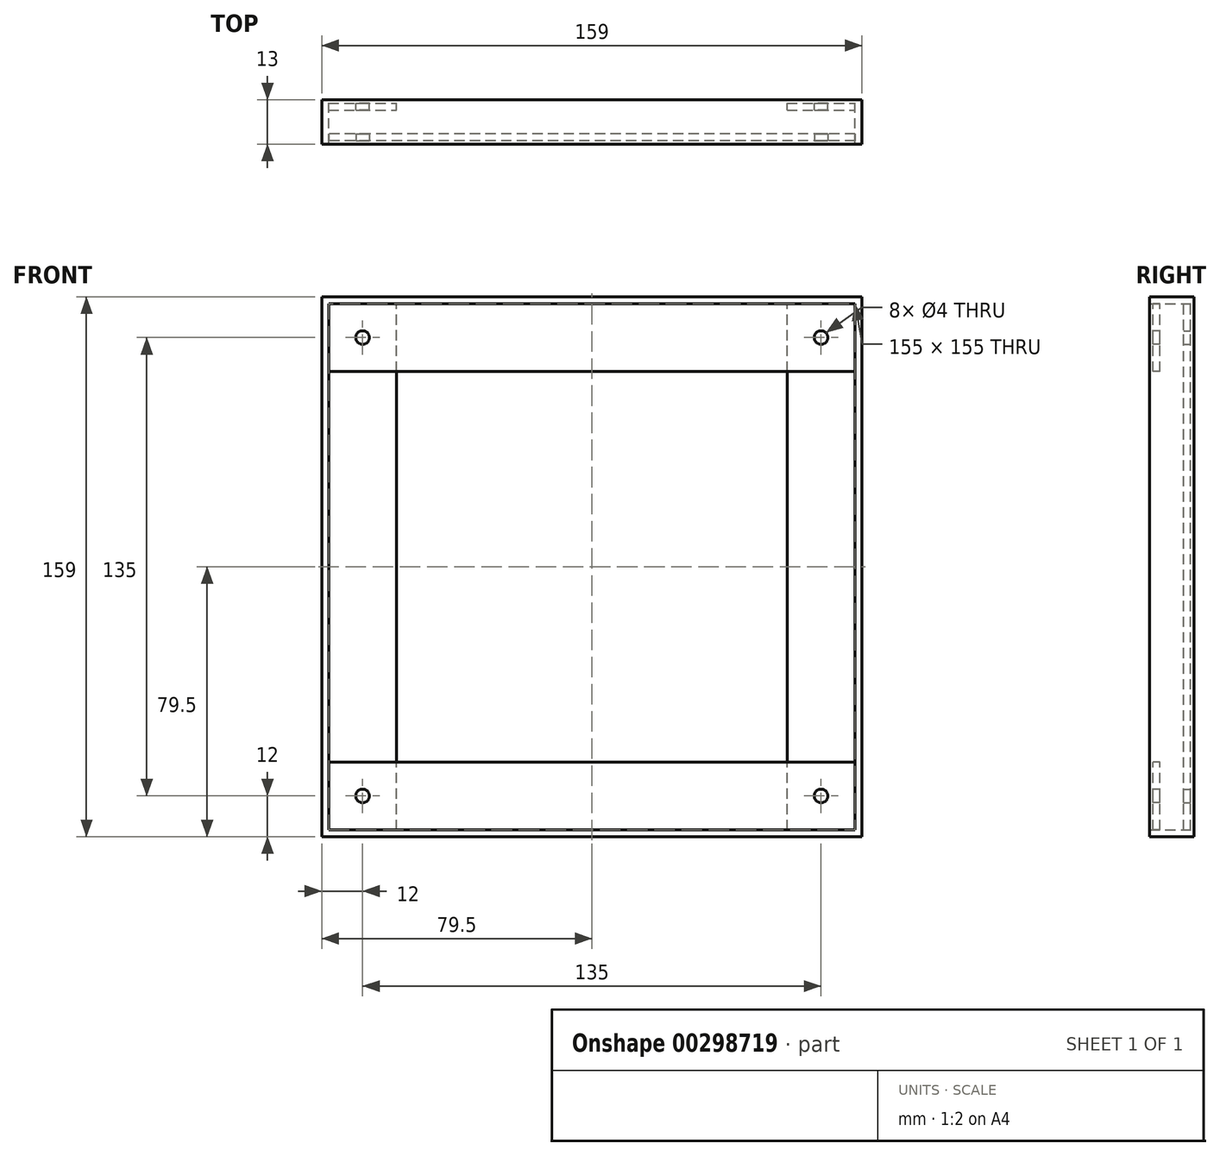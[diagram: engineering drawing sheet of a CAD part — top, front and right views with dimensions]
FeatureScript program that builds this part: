
annotation { "Feature Type Name" : "Feature", "Feature Type Description" : "" }
export const myFeature = defineFeature(function(context is Context, id is Id, definition is map)
    precondition{}
    {
        {
            var Q0;
            Q0=qCreatedBy(makeId("Front.planeOp"),FACE);
            var sketch = newSketch(context, id + "F0", { "sketchPlane" : qUnion([Q0])});
            skLineSegment(sketch, "E0.bottom", {"start": v(0, 0) * mm, "end": v(155, 0) * mm});
            skLineSegment(sketch, "E0.top", {"start": v(0, 155) * mm, "end": v(155, 155) * mm});
            skLineSegment(sketch, "E0.left", {"start": v(0, 0) * mm, "end": v(0, 155) * mm});
            skLineSegment(sketch, "E0.right", {"start": v(155, 0) * mm, "end": v(155, 155) * mm});
            skLineSegment(sketch, "E1.bottom", {"start": v(-2, 157) * mm, "end": v(157, 157) * mm});
            skLineSegment(sketch, "E1.top", {"start": v(-2, -2) * mm, "end": v(157, -2) * mm});
            skLineSegment(sketch, "E1.left", {"start": v(-2, 157) * mm, "end": v(-2, -2) * mm});
            skLineSegment(sketch, "E1.right", {"start": v(157, 157) * mm, "end": v(157, -2) * mm});
            skSolve(sketch);
        }
        {
            var Q0;
            Q0=makeQuery(id+"F0.imprint","IMPRINT",FACE,{"disambiguationData":[TD([[makeQuery(id+"F0.imprint","IMPRINT",EDGE,{"derivedFrom":sQuery(id+"F0.wireOp",EDGE,"E0.bottom")}),-1.0]])]});
            extrude(context, id + "F1", {"entities" : qUnion([Q0]), "depth" : 13 * mm});
        }
        {
            var Q0;
            Q0=qCreatedBy(makeId("Front.planeOp"),FACE);
            cPlane(context, id + "F2", {"entities" : qUnion([Q0]), "cplaneType" : CPlaneType.OFFSET, "offset" : 1 * mm, "width" : 150 * mm, "height" : 150 * mm});
        }
        {
            var Q0;
            Q0=qCreatedBy(id+"F2.planeOp",FACE);
            var sketch = newSketch(context, id + "F3", { "sketchPlane" : qUnion([Q0])});
            skLineSegment(sketch, "E2.0", {"start": v(0, 155) * mm, "end": v(155, 155) * mm});
            skLineSegment(sketch, "E2.1", {"start": v(0, 0) * mm, "end": v(0, 155) * mm});
            skLineSegment(sketch, "E2.2", {"start": v(0, 0) * mm, "end": v(155, 0) * mm});
            skLineSegment(sketch, "E2.3", {"start": v(155, 0) * mm, "end": v(155, 155) * mm});
            skLineSegment(sketch, "E3", {"start": v(20, 0) * mm, "end": v(20, 155) * mm});
            skCircle(sketch, "E4", {"center": v(10, 145) * mm, "radius": 2 * mm});
            skCircle(sketch, "E5", {"center": v(10, 10) * mm, "radius": 2 * mm});
            skLineSegment(sketch, "E6", {"start": v(0, 77.5) * mm, "end": v(155, 77.5) * mm, "construction": true});
            skLineSegment(sketch, "E7", {"start": v(77.5, 0) * mm, "end": v(77.5, 155) * mm, "construction": true});
            skLineSegment(sketch, "E8", {"start": v(135, 0) * mm, "end": v(135, 155) * mm});
            skCircle(sketch, "E9", {"center": v(145, 10) * mm, "radius": 2 * mm});
            skCircle(sketch, "E10", {"center": v(145, 145) * mm, "radius": 2 * mm});
            skSolve(sketch);
        }
        {
            var Q0;
            {var subQ1=sQuery(id+"F3.wireOp",EDGE,"E2.1");Q0=makeQuery(id+"F3.imprint","IMPRINT",FACE,{"disambiguationData":[TD([[makeQuery(id+"F3.imprint","IMPRINT",EDGE,{"derivedFrom":subQ1}),-1.0]])]});}
            var Q1;
            {var subQ1=sQuery(id+"F3.wireOp",EDGE,"E2.3");Q1=makeQuery(id+"F3.imprint","IMPRINT",FACE,{"disambiguationData":[TD([[makeQuery(id+"F3.imprint","IMPRINT",EDGE,{"derivedFrom":subQ1}),1.0]])]});}
            extrude(context, id + "F4", {"entities" : qUnion([Q0, Q1]), "depth" : 2 * mm});
        }
        {
            var Q0;
            Q0=makeQuery(id+"F1.opExtrude","CAP_FACE",FACE,{"disambiguationData":[OSD([sQuery(id+"F0.wireOp",EDGE,"E0.bottom"),sQuery(id+"F0.wireOp",EDGE,"E0.top"),sQuery(id+"F0.wireOp",EDGE,"E0.left"),sQuery(id+"F0.wireOp",EDGE,"E0.right"),sQuery(id+"F0.wireOp",EDGE,"E1.bottom"),sQuery(id+"F0.wireOp",EDGE,"E1.top"),sQuery(id+"F0.wireOp",EDGE,"E1.left"),sQuery(id+"F0.wireOp",EDGE,"E1.right")])],"isStart":false});
            cPlane(context, id + "F5", {"entities" : qUnion([Q0]), "cplaneType" : CPlaneType.OFFSET, "offset" : 1 * mm, "oppositeDirection" : true, "width" : 150 * mm, "height" : 150 * mm});
        }
        {
            var Q0;
            Q0=qCreatedBy(id+"F5.planeOp",FACE);
            var sketch = newSketch(context, id + "F6", { "sketchPlane" : qUnion([Q0])});
            skLineSegment(sketch, "E11.0", {"start": v(0, 0) * mm, "end": v(155, 0) * mm});
            skLineSegment(sketch, "E11.1", {"start": v(155, 0) * mm, "end": v(155, 155) * mm});
            skLineSegment(sketch, "E11.2", {"start": v(0, 155) * mm, "end": v(155, 155) * mm});
            skLineSegment(sketch, "E11.3", {"start": v(0, 0) * mm, "end": v(0, 155) * mm});
            skLineSegment(sketch, "E12", {"start": v(155, 20) * mm, "end": v(0, 20) * mm});
            skCircle(sketch, "E13.0", {"center": v(145, 10) * mm, "radius": 2 * mm});
            skCircle(sketch, "E13.1", {"center": v(10, 10) * mm, "radius": 2 * mm});
            skCircle(sketch, "E13.2", {"center": v(10, 145) * mm, "radius": 2 * mm});
            skCircle(sketch, "E13.3", {"center": v(145, 145) * mm, "radius": 2 * mm});
            skLineSegment(sketch, "E14", {"start": v(155, 135) * mm, "end": v(0, 135) * mm});
            skSolve(sketch);
        }
        {
            var Q0;
            {var subQ1=sQuery(id+"F6.wireOp",EDGE,"E11.2");Q0=makeQuery(id+"F6.imprint","IMPRINT",FACE,{"disambiguationData":[TD([[makeQuery(id+"F6.imprint","IMPRINT",EDGE,{"derivedFrom":subQ1}),-1.0]])]});}
            var Q1;
            {var subQ2=sQuery(id+"F6.wireOp",EDGE,"E11.0");Q1=makeQuery(id+"F6.imprint","IMPRINT",FACE,{"disambiguationData":[TD([[makeQuery(id+"F6.imprint","IMPRINT",EDGE,{"derivedFrom":subQ2}),1.0]])]});}
            extrude(context, id + "F7", {"entities" : qUnion([Q0, Q1]), "oppositeDirection" : true, "depth" : 2 * mm});
        }
    });
